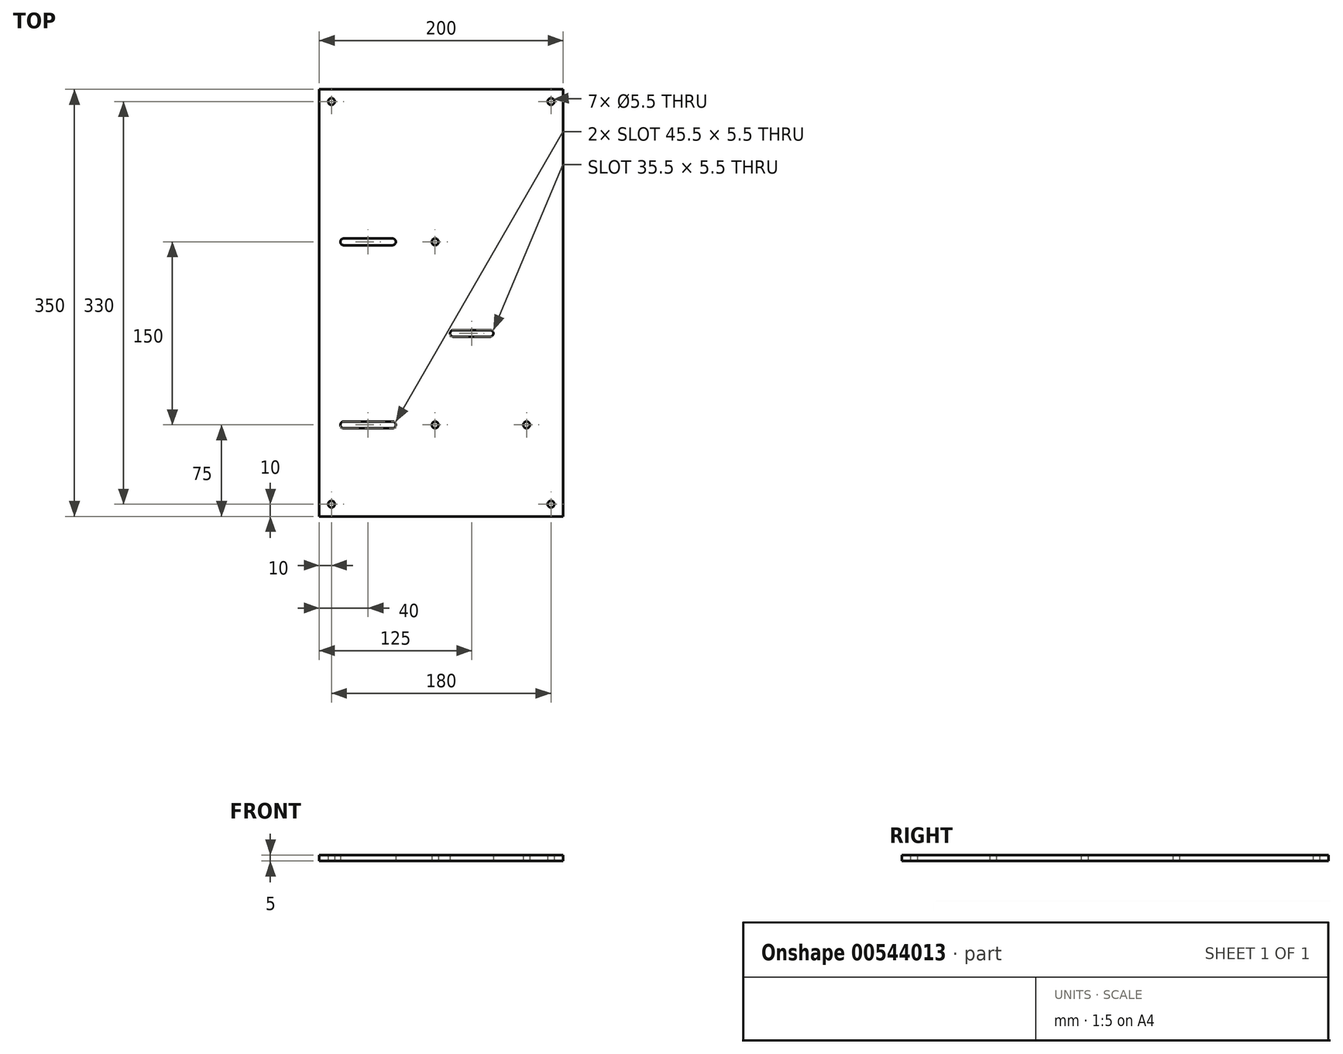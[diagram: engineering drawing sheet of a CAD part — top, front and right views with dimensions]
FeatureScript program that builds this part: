
annotation { "Feature Type Name" : "Feature", "Feature Type Description" : "" }
export const myFeature = defineFeature(function(context is Context, id is Id, definition is map)
    precondition{}
    {
        {
            var Q0;
            Q0=qCreatedBy(makeId("Top.planeOp"),FACE);
            var sketch = newSketch(context, id + "F0", { "sketchPlane" : qUnion([Q0])});
            skLineSegment(sketch, "E0.bottom", {"start": v(100, -175) * mm, "end": v(-100, -175) * mm});
            skLineSegment(sketch, "E0.top", {"start": v(100, 175) * mm, "end": v(-100, 175) * mm});
            skLineSegment(sketch, "E0.left", {"start": v(100, -175) * mm, "end": v(100, 175) * mm});
            skLineSegment(sketch, "E0.right", {"start": v(-100, -175) * mm, "end": v(-100, 175) * mm});
            skPoint(sketch, "E0.middle", {"position": v(0, 0) * mm});
            skArc(sketch, "E1", {"start": v(-80, -97.25) * mm, "mid": v(-82.75, -100) * mm, "end": v(-80, -102.75) * mm});
            skLineSegment(sketch, "E2.bottom", {"start": v(-80, -97.25) * mm, "end": v(-60, -97.25) * mm});
            skLineSegment(sketch, "E2.top", {"start": v(-80, -102.75) * mm, "end": v(-60, -102.75) * mm});
            skLineSegment(sketch, "E3", {"start": v(-60, -97.25) * mm, "end": v(-60, -102.75) * mm, "construction": true});
            skLineSegment(sketch, "E4.MirrorCS", {"start": v(-40, -97.25) * mm, "end": v(-60, -97.25) * mm});
            skLineSegment(sketch, "E5.MirrorCS", {"start": v(-40, -102.75) * mm, "end": v(-60, -102.75) * mm});
            skArc(sketch, "E6.MirrorCS", {"start": v(-40, -97.25) * mm, "mid": v(-37.25, -100) * mm, "end": v(-40, -102.75) * mm});
            skCircle(sketch, "E7", {"center": v(-5, -100) * mm, "radius": 2.75 * mm});
            skCircle(sketch, "E8", {"center": v(70, -100) * mm, "radius": 2.75 * mm});
            skCircle(sketch, "E9.0.1.0", {"center": v(-5, 50) * mm, "radius": 2.75 * mm});
            skLineSegment(sketch, "E9.direction1", {"start": v(-5, -100) * mm, "end": v(20, -100) * mm, "construction": true});
            skLineSegment(sketch, "E9.direction2", {"start": v(-5, -100) * mm, "end": v(-5, 50) * mm, "construction": true});
            skLineSegment(sketch, "E10.0.1.0", {"start": v(-40, 47.25) * mm, "end": v(-60, 47.25) * mm});
            skLineSegment(sketch, "E10.0.1.1", {"start": v(-80, 52.75) * mm, "end": v(-60, 52.75) * mm});
            skArc(sketch, "E10.0.1.2", {"start": v(-80, 52.75) * mm, "mid": v(-82.75, 50) * mm, "end": v(-80, 47.25) * mm});
            skLineSegment(sketch, "E10.0.1.3", {"start": v(-80, 47.25) * mm, "end": v(-60, 47.25) * mm});
            skLineSegment(sketch, "E10.0.1.4", {"start": v(-40, 52.75) * mm, "end": v(-60, 52.75) * mm});
            skArc(sketch, "E10.0.1.5", {"start": v(-40, 52.75) * mm, "mid": v(-37.25, 50) * mm, "end": v(-40, 47.25) * mm});
            skLineSegment(sketch, "E10.direction1", {"start": v(-60, -102.75) * mm, "end": v(-35, -102.75) * mm, "construction": true});
            skLineSegment(sketch, "E10.direction2", {"start": v(-60, -102.75) * mm, "end": v(-60, 47.25) * mm, "construction": true});
            skLineSegment(sketch, "E11.0.1.0", {"start": v(40, -27.75) * mm, "end": v(25, -27.75) * mm});
            skLineSegment(sketch, "E11.0.1.1", {"start": v(10, -22.25) * mm, "end": v(25, -22.25) * mm});
            skArc(sketch, "E11.0.1.2", {"start": v(10, -22.25) * mm, "mid": v(7.25, -25) * mm, "end": v(10, -27.75) * mm});
            skLineSegment(sketch, "E11.0.1.3", {"start": v(10, -27.75) * mm, "end": v(25, -27.75) * mm});
            skLineSegment(sketch, "E11.0.1.4", {"start": v(40, -22.25) * mm, "end": v(25, -22.25) * mm});
            skArc(sketch, "E11.0.1.5", {"start": v(40, -22.25) * mm, "mid": v(42.75, -25) * mm, "end": v(40, -27.75) * mm});
            skCircle(sketch, "E12", {"center": v(-90, -165) * mm, "radius": 2.75 * mm});
            skCircle(sketch, "E13.0.1.0", {"center": v(-90, 165) * mm, "radius": 2.75 * mm});
            skCircle(sketch, "E13.1.0.0", {"center": v(90, -165) * mm, "radius": 2.75 * mm});
            skCircle(sketch, "E13.1.1.0", {"center": v(90, 165) * mm, "radius": 2.75 * mm});
            skLineSegment(sketch, "E13.direction1", {"start": v(-90, -165) * mm, "end": v(90, -165) * mm, "construction": true});
            skLineSegment(sketch, "E13.direction2", {"start": v(-90, -165) * mm, "end": v(-90, 165) * mm, "construction": true});
            skSolve(sketch);
        }
        {
            var Q0;
            Q0 = qSketchRegion(id + "F0", true);
            extrude(context, id + "F1", {"entities" : qUnion([Q0]), "depth" : 5 * mm, "offsetDistance" : 25 * mm});
        }
    });
